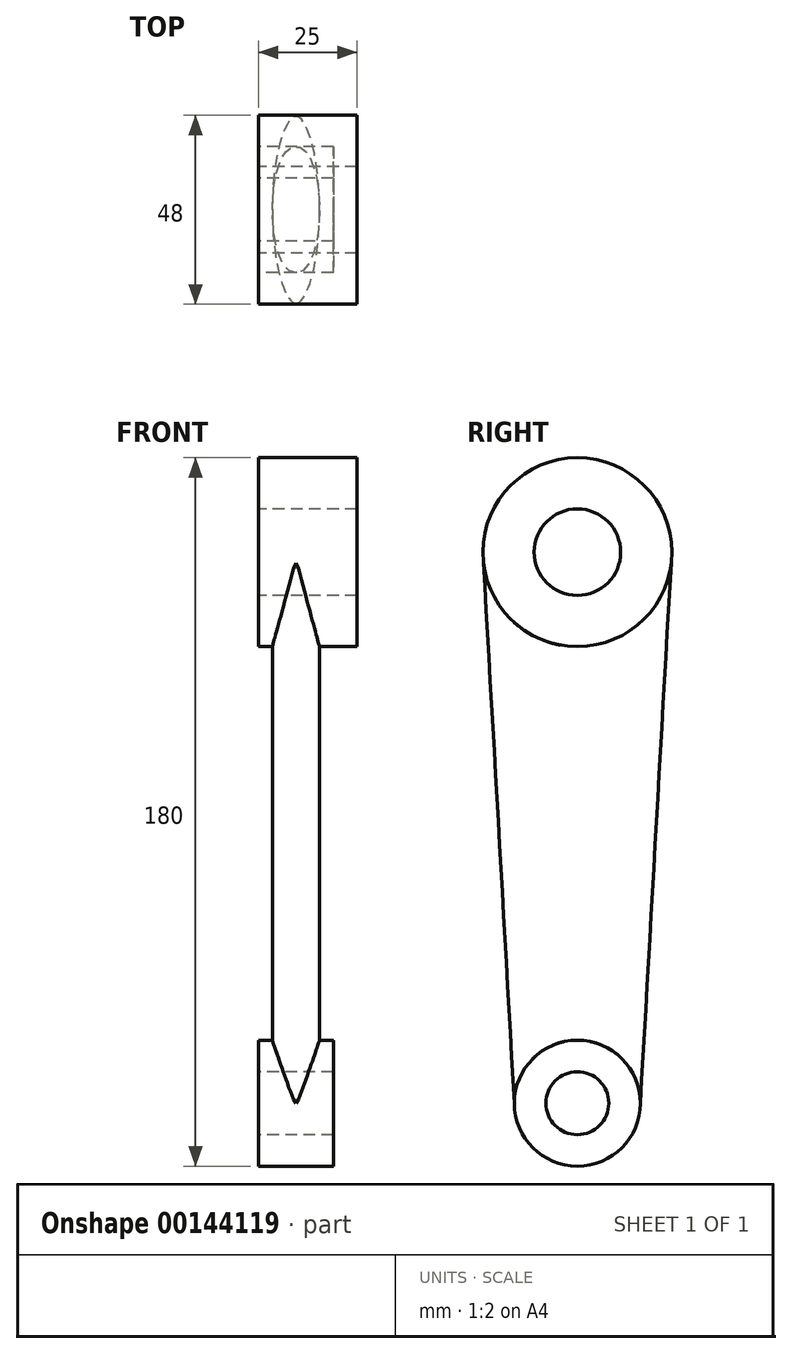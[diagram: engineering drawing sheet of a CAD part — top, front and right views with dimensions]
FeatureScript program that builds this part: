
annotation { "Feature Type Name" : "Feature", "Feature Type Description" : "" }
export const myFeature = defineFeature(function(context is Context, id is Id, definition is map)
    precondition{}
    {
        {
            var Q0;
            Q0=qCreatedBy(makeId("Right.planeOp"),FACE);
            var sketch = newSketch(context, id + "F0", { "sketchPlane" : qUnion([Q0])});
            skCircle(sketch, "E0", {"center": v(0, 0) * mm, "radius": 8 * mm});
            skCircle(sketch, "E1", {"center": v(0, 0) * mm, "radius": 16 * mm});
            skCircle(sketch, "E2", {"center": v(0, 140) * mm, "radius": 11 * mm});
            skCircle(sketch, "E3", {"center": v(0, 140) * mm, "radius": 24 * mm});
            skLineSegment(sketch, "E4", {"start": v(23.96, 138.63) * mm, "end": v(16.03, 0) * mm});
            skLineSegment(sketch, "E5", {"start": v(-16, 0) * mm, "end": v(-23.96, 138.62) * mm});
            skSolve(sketch);
        }
        {
            var Q0;
            Q0=makeQuery(id+"F0.imprint","IMPRINT",FACE,{"disambiguationData":[TD([[makeQuery(id+"F0.imprint","IMPRINT",EDGE,{"derivedFrom":sQuery(id+"F0.wireOp",EDGE,"E0")}),1.0]])]});
            var Q1;
            Q1=makeQuery(id+"F0.imprint","IMPRINT",FACE,{"disambiguationData":[TD([[makeQuery(id+"F0.imprint","IMPRINT",EDGE,{"derivedFrom":sQuery(id+"F0.wireOp",EDGE,"E0")}),-1.0]])]});
            var Q2;
            Q2=sQuery(id+"F0.wireOp",EDGE,"E1");
            var Q3;
            Q3=sQuery(id+"F0.wireOp",EDGE,"E0");
            extrude(context, id + "F1", {"entities" : qUnion([Q0, Q1]), "surfaceEntities" : qUnion([Q2, Q3]), "depth" : 19 * mm});
        }
        {
            var Q0;
            Q0=makeQuery(id+"F0.imprint","IMPRINT",FACE,{"disambiguationData":[TD([[makeQuery(id+"F0.imprint","IMPRINT",EDGE,{"derivedFrom":sQuery(id+"F0.wireOp",EDGE,"E2")}),1.0]])]});
            var Q1;
            Q1=makeQuery(id+"F0.imprint","IMPRINT",FACE,{"disambiguationData":[TD([[makeQuery(id+"F0.imprint","IMPRINT",EDGE,{"derivedFrom":sQuery(id+"F0.wireOp",EDGE,"E2")}),-1.0]])]});
            extrude(context, id + "F2", {"entities" : qUnion([Q0, Q1]), "depth" : 25 * mm});
        }
        {
            var Q0;
            Q0=qCreatedBy(makeId("Top.planeOp"),FACE);
            var sketch = newSketch(context, id + "F3", { "sketchPlane" : qUnion([Q0])});
            skEllipse(sketch, "E6", {"center": v(9.5, 0) * mm, "majorRadius": 16 * mm, "minorRadius": 6 * mm, "majorAxis": v(0, 1)});
            skLineSegment(sketch, "E7", {"start": v(0, 16) * mm, "end": v(19, 16) * mm, "construction": true});
            skPoint(sketch, "E8", {"position": v(3.5, 0) * mm});
            skSolve(sketch);
        }
        {
            var Q0;
            Q0=makeQuery(id+"F2.opExtrude","CAP_FACE",FACE,{"disambiguationData":[OSD([sQuery(id+"F0.wireOp",EDGE,"E3")])],"isStart":true});
            var sketch = newSketch(context, id + "F4", { "sketchPlane" : qUnion([Q0])});
            skCircle(sketch, "E9", {"center": v(0, 140) * mm, "radius": 24 * mm, "construction": true});
            skSolve(sketch);
        }
        {
            var Q0;
            Q0=sQuery(id+"F4.wireOp",VERTEX,"E9.center");
            var Q1;
            Q1=qCreatedBy(makeId("Top.planeOp"),FACE);
            cPlane(context, id + "F5", {"entities" : qUnion([Q0, Q1]), "cplaneType" : CPlaneType.PLANE_POINT, "offset" : 25 * mm, "oppositeDirection" : true, "width" : 150 * mm, "height" : 150 * mm});
        }
        {
            var Q0;
            Q0=qCreatedBy(id+"F5.planeOp",FACE);
            var sketch = newSketch(context, id + "F6", { "sketchPlane" : qUnion([Q0])});
            skEllipse(sketch, "E10", {"center": v(9.5, 0) * mm, "majorRadius": 24 * mm, "minorRadius": 6 * mm, "majorAxis": v(0, -1)});
            skPoint(sketch, "E11", {"position": v(3.5, 0) * mm});
            skLineSegment(sketch, "E12", {"start": v(0, 24) * mm, "end": v(25, 24) * mm, "construction": true});
            skSolve(sketch);
        }
        {
            var Q0;
            Q0=makeQuery(id+"F6.imprint","IMPRINT",FACE,{"disambiguationData":[TD([[makeQuery(id+"F6.imprint","IMPRINT",EDGE,{"derivedFrom":sQuery(id+"F6.wireOp",EDGE,"E10")}),1.0]])]});
            var Q1;
            Q1=makeQuery(id+"F3.imprint","IMPRINT",FACE,{"disambiguationData":[TD([[makeQuery(id+"F3.imprint","IMPRINT",EDGE,{"derivedFrom":sQuery(id+"F3.wireOp",EDGE,"E6")}),1.0]])]});
            loft(context, id + "F7", {"operationType" : NewBodyOperationType.ADD, "sheetProfilesArray" : [{ "sheetProfileEntities" : qUnion([Q0]) }, { "sheetProfileEntities" : qUnion([Q1]) }]});
        }
        {
            var Q0;
            Q0=makeQuery(id+"F0.imprint","IMPRINT",FACE,{"disambiguationData":[TD([[makeQuery(id+"F0.imprint","IMPRINT",EDGE,{"derivedFrom":sQuery(id+"F0.wireOp",EDGE,"E2")}),1.0]])]});
            var Q1;
            Q1=makeQuery(id+"F0.imprint","IMPRINT",FACE,{"disambiguationData":[TD([[makeQuery(id+"F0.imprint","IMPRINT",EDGE,{"derivedFrom":sQuery(id+"F0.wireOp",EDGE,"E0")}),1.0]])]});
            extrude(context, id + "F8", {"entities" : qUnion([Q0, Q1]), "operationType" : NewBodyOperationType.REMOVE, "endBound" : BoundingType.THROUGH_ALL, "depth" : 25 * mm});
        }
        {
            var Q0;
            Q0=qCreatedBy(makeId("Right.planeOp"),FACE);
            cPlane(context, id + "F9", {"entities" : qUnion([Q0]), "cplaneType" : CPlaneType.OFFSET, "offset" : 9.5 * mm, "width" : 150 * mm, "height" : 150 * mm});
        }
    });
